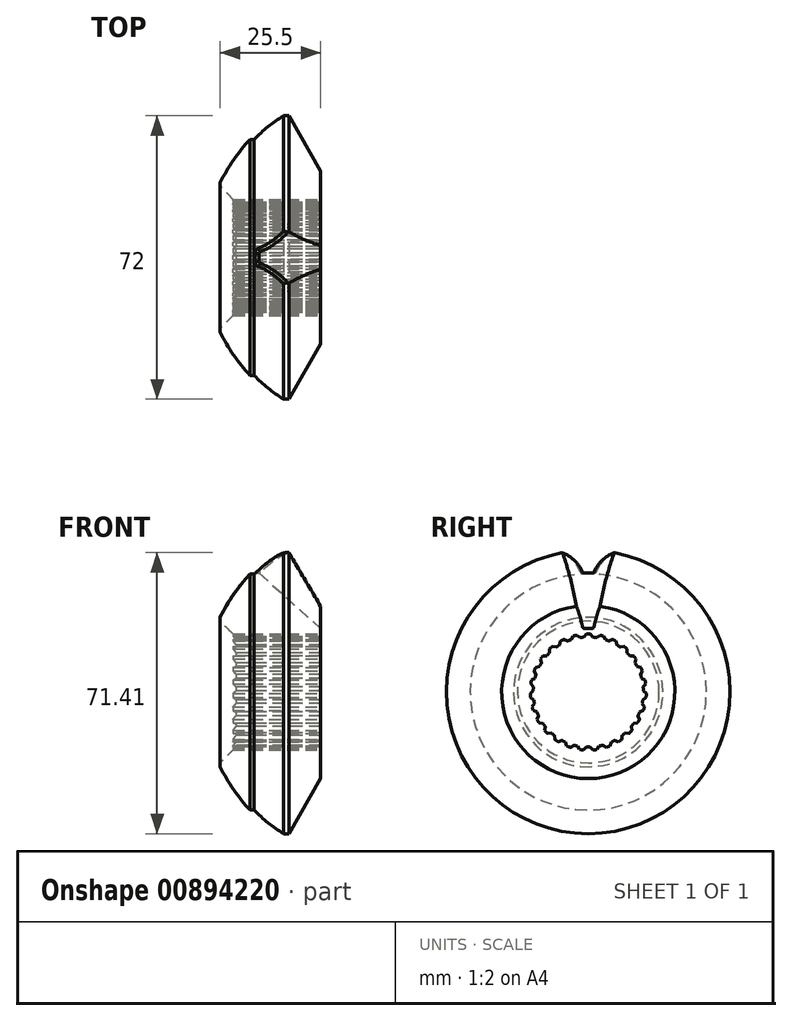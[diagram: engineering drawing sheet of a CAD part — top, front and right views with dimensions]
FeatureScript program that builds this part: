
annotation { "Feature Type Name" : "Feature", "Feature Type Description" : "" }
export const myFeature = defineFeature(function(context is Context, id is Id, definition is map)
    precondition{}
    {
        {
            var Q0;
            Q0=qCreatedBy(makeId("Front.planeOp"),FACE);
            var sketch = newSketch(context, id + "F0", { "sketchPlane" : qUnion([Q0])});
            skLineSegment(sketch, "E0", {"start": v(-35.13, 14) * mm, "end": v(-13.63, 14) * mm});
            skLineSegment(sketch, "E1", {"start": v(-13.63, 14) * mm, "end": v(-13.63, 22) * mm});
            skLineSegment(sketch, "E2", {"start": v(-13.63, 22) * mm, "end": v(-21.71, 36) * mm});
            skLineSegment(sketch, "E3", {"start": v(-21.71, 36) * mm, "end": v(-23.11, 36) * mm});
            skLineSegment(sketch, "E4", {"start": v(-35.13, 14) * mm, "end": v(-39.13, 18) * mm});
            skLineSegment(sketch, "E5", {"start": v(-39.13, 18) * mm, "end": v(-39.13, 19) * mm});
            skArc(sketch, "E6", {"start": v(-31.5, 30) * mm, "mid": v(-35.74, 24.8) * mm, "end": v(-39.13, 19) * mm});
            skLineSegment(sketch, "E7", {"start": v(-31.5, 30) * mm, "end": v(-30.5, 30) * mm});
            skArc(sketch, "E8", {"start": v(-23.11, 36) * mm, "mid": v(-26.97, 33.2) * mm, "end": v(-30.5, 30) * mm});
            skLineSegment(sketch, "E9", {"start": v(-39.13, 0) * mm, "end": v(0, 0) * mm});
            skSolve(sketch);
        }
        {
            var Q0;
            Q0=makeQuery(id+"F0.imprint","IMPRINT",FACE,{"disambiguationData":[TD([[makeQuery(id+"F0.imprint","IMPRINT",EDGE,{"derivedFrom":sQuery(id+"F0.wireOp",EDGE,"E0")}),1.0]])]});
            var Q1;
            Q1=sQuery(id+"F0.wireOp",EDGE,"E9");
            revolve(context, id + "F1", {"surfaceOperationType" : NewSurfaceOperationType.NEW, "entities" : qUnion([Q0]), "axis" : qUnion([Q1]), "revolveType" : RevolveType.FULL});
        }
        {
            var Q0;
            Q0=makeQuery(id+"F1.opRevolve","SWEPT_FACE",FACE,{"disambiguationData":[OSD([sQuery(id+"F0.wireOp",EDGE,"E1")])]});
            var sketch = newSketch(context, id + "F2", { "sketchPlane" : qUnion([Q0])});
            skLineSegment(sketch, "E10", {"start": v(0, 0) * mm, "end": v(0, 16.12) * mm, "construction": true});
            skLineSegment(sketch, "E11", {"start": v(0, 16.12) * mm, "end": v(20, 16.12) * mm, "construction": true});
            skSolve(sketch);
        }
        {
            var Q0;
            Q0=sQuery(id+"F2.wireOp",EDGE,"E11");
            var Q1;
            {var subQ0=sQuery(id+"F0.wireOp",EDGE,"E1");Q1=makeQuery(id+"F2.imprint","IMPRINT",FACE,{"disambiguationData":[TD([[makeQuery(id+"F2.imprint","IMPRINT",EDGE,{"derivedFrom":makeQuery(id+"F1.opRevolve","SWEPT_EDGE",EDGE,{"disambiguationData":[OSD([sQuery(id+"F0.wireOp",EDGE,"E0"),subQ0])]})}),1.0]])]});}
            cPlane(context, id + "F3", {"entities" : qUnion([Q0, Q1]), "cplaneType" : CPlaneType.LINE_ANGLE, "offset" : 25 * mm, "angle" : 42 * degree, "width" : 150 * mm, "height" : 150 * mm});
        }
        {
            var Q0;
            Q0=qCreatedBy(id+"F3.planeOp",FACE);
            var sketch = newSketch(context, id + "F4", { "sketchPlane" : qUnion([Q0])});
            skLineSegment(sketch, "E12", {"start": v(0, 2.86) * mm, "end": v(0, 7.08) * mm, "construction": true});
            skLineSegment(sketch, "E13", {"start": v(3, 7.08) * mm, "end": v(-3, 7.08) * mm, "construction": true});
            skLineSegment(sketch, "E14", {"start": v(6.55, 11.78) * mm, "end": v(-6.55, 11.78) * mm, "construction": true});
            skLineSegment(sketch, "E15", {"start": v(0, 7.08) * mm, "end": v(0, 11.78) * mm, "construction": true});
            skArc(sketch, "E16", {"start": v(-1.48, 3.23) * mm, "mid": v(-2.13, 5.2) * mm, "end": v(-3, 7.08) * mm});
            skArc(sketch, "E17", {"start": v(-3, 7.08) * mm, "mid": v(-4.59, 9.57) * mm, "end": v(-6.55, 11.78) * mm});
            skArc(sketch, "E18", {"start": v(-1.48, 3.23) * mm, "mid": v(-1.3, 2.97) * mm, "end": v(-1, 2.86) * mm});
            skLineSegment(sketch, "E19", {"start": v(-1, 2.86) * mm, "end": v(1, 2.86) * mm});
            skLineSegment(sketch, "E20", {"start": v(-6.55, 11.78) * mm, "end": v(-6.55, 12.78) * mm});
            skLineSegment(sketch, "E21", {"start": v(-6.55, 12.78) * mm, "end": v(6.55, 12.78) * mm});
            skLineSegment(sketch, "E22", {"start": v(6.55, 12.78) * mm, "end": v(6.55, 11.78) * mm});
            skArc(sketch, "E23", {"start": v(1, 2.86) * mm, "mid": v(1.3, 2.97) * mm, "end": v(1.48, 3.23) * mm});
            skArc(sketch, "E24", {"start": v(3, 7.08) * mm, "mid": v(2.13, 5.2) * mm, "end": v(1.48, 3.23) * mm});
            skArc(sketch, "E25", {"start": v(6.55, 11.78) * mm, "mid": v(4.59, 9.57) * mm, "end": v(3, 7.08) * mm});
            skSolve(sketch);
        }
        {
            var Q0;
            Q0=makeQuery(id+"F4.imprint","IMPRINT",FACE,{"disambiguationData":[TD([[makeQuery(id+"F4.imprint","IMPRINT",EDGE,{"derivedFrom":sQuery(id+"F4.wireOp",EDGE,"E16")}),-1.0]])]});
            extrude(context, id + "F5", {"entities" : qUnion([Q0]), "operationType" : NewBodyOperationType.REMOVE, "endBound" : BoundingType.THROUGH_ALL, "depth" : 25 * mm, "offsetDistance" : 25 * mm});
        }
        {
            var Q0;
            Q0=makeQuery(id+"F5.boolean.opBoolean","INTERSECT",EDGE,{"derivedFrom":[makeQuery(id+"F1.opRevolve","SWEPT_FACE",FACE,{"disambiguationData":[OSD([sQuery(id+"F0.wireOp",EDGE,"E8")])]}),makeQuery(id+"F5.opExtrude","SWEPT_FACE",FACE,{"disambiguationData":[OSD([sQuery(id+"F4.wireOp",EDGE,"E16"),sQuery(id+"F4.wireOp",EDGE,"E17")])]})]});
            var Q1;
            Q1=makeQuery(id+"Ff50wVPIjlx40M6_1.1.F5.boolean.opBoolean","INTERSECT",EDGE,{"derivedFrom":[makeQuery(id+"F1.opRevolve","SWEPT_FACE",FACE,{"disambiguationData":[OSD([sQuery(id+"F0.wireOp",EDGE,"E8")])]}),makeQuery(id+"Ff50wVPIjlx40M6_1.1.F5.opExtrude","SWEPT_FACE",FACE,{"disambiguationData":[OSD([sQuery(id+"F4.wireOp",EDGE,"E16"),sQuery(id+"F4.wireOp",EDGE,"E17")])]})]});
            var Q2;
            Q2=makeQuery(id+"Ff50wVPIjlx40M6_1.2.F5.boolean.opBoolean","INTERSECT",EDGE,{"derivedFrom":[makeQuery(id+"F1.opRevolve","SWEPT_FACE",FACE,{"disambiguationData":[OSD([sQuery(id+"F0.wireOp",EDGE,"E8")])]}),makeQuery(id+"Ff50wVPIjlx40M6_1.2.F5.opExtrude","SWEPT_FACE",FACE,{"disambiguationData":[OSD([sQuery(id+"F4.wireOp",EDGE,"E16"),sQuery(id+"F4.wireOp",EDGE,"E17")])]})]});
            var Q3;
            Q3=makeQuery(id+"Ff50wVPIjlx40M6_1.3.F5.boolean.opBoolean","INTERSECT",EDGE,{"derivedFrom":[makeQuery(id+"F1.opRevolve","SWEPT_FACE",FACE,{"disambiguationData":[OSD([sQuery(id+"F0.wireOp",EDGE,"E8")])]}),makeQuery(id+"Ff50wVPIjlx40M6_1.3.F5.opExtrude","SWEPT_FACE",FACE,{"disambiguationData":[OSD([sQuery(id+"F4.wireOp",EDGE,"E16"),sQuery(id+"F4.wireOp",EDGE,"E17")])]})]});
            var Q4;
            Q4=makeQuery(id+"Ff50wVPIjlx40M6_1.4.F5.boolean.opBoolean","INTERSECT",EDGE,{"derivedFrom":[makeQuery(id+"F1.opRevolve","SWEPT_FACE",FACE,{"disambiguationData":[OSD([sQuery(id+"F0.wireOp",EDGE,"E8")])]}),makeQuery(id+"Ff50wVPIjlx40M6_1.4.F5.opExtrude","SWEPT_FACE",FACE,{"disambiguationData":[OSD([sQuery(id+"F4.wireOp",EDGE,"E16"),sQuery(id+"F4.wireOp",EDGE,"E17")])]})]});
            var Q5;
            Q5=makeQuery(id+"Ff50wVPIjlx40M6_1.5.F5.boolean.opBoolean","INTERSECT",EDGE,{"derivedFrom":[makeQuery(id+"F1.opRevolve","SWEPT_FACE",FACE,{"disambiguationData":[OSD([sQuery(id+"F0.wireOp",EDGE,"E8")])]}),makeQuery(id+"Ff50wVPIjlx40M6_1.5.F5.opExtrude","SWEPT_FACE",FACE,{"disambiguationData":[OSD([sQuery(id+"F4.wireOp",EDGE,"E16"),sQuery(id+"F4.wireOp",EDGE,"E17")])]})]});
            var Q6;
            Q6=makeQuery(id+"Ff50wVPIjlx40M6_1.6.F5.boolean.opBoolean","INTERSECT",EDGE,{"derivedFrom":[makeQuery(id+"F1.opRevolve","SWEPT_FACE",FACE,{"disambiguationData":[OSD([sQuery(id+"F0.wireOp",EDGE,"E8")])]}),makeQuery(id+"Ff50wVPIjlx40M6_1.6.F5.opExtrude","SWEPT_FACE",FACE,{"disambiguationData":[OSD([sQuery(id+"F4.wireOp",EDGE,"E16"),sQuery(id+"F4.wireOp",EDGE,"E17")])]})]});
            var Q7;
            Q7=makeQuery(id+"Ff50wVPIjlx40M6_1.7.F5.boolean.opBoolean","INTERSECT",EDGE,{"derivedFrom":[makeQuery(id+"F1.opRevolve","SWEPT_FACE",FACE,{"disambiguationData":[OSD([sQuery(id+"F0.wireOp",EDGE,"E8")])]}),makeQuery(id+"Ff50wVPIjlx40M6_1.7.F5.opExtrude","SWEPT_FACE",FACE,{"disambiguationData":[OSD([sQuery(id+"F4.wireOp",EDGE,"E16"),sQuery(id+"F4.wireOp",EDGE,"E17")])]})]});
            var Q8;
            Q8=makeQuery(id+"Ff50wVPIjlx40M6_1.8.F5.boolean.opBoolean","INTERSECT",EDGE,{"derivedFrom":[makeQuery(id+"F1.opRevolve","SWEPT_FACE",FACE,{"disambiguationData":[OSD([sQuery(id+"F0.wireOp",EDGE,"E8")])]}),makeQuery(id+"Ff50wVPIjlx40M6_1.8.F5.opExtrude","SWEPT_FACE",FACE,{"disambiguationData":[OSD([sQuery(id+"F4.wireOp",EDGE,"E16"),sQuery(id+"F4.wireOp",EDGE,"E17")])]})]});
            var Q9;
            Q9=makeQuery(id+"Ff50wVPIjlx40M6_1.9.F5.boolean.opBoolean","INTERSECT",EDGE,{"derivedFrom":[makeQuery(id+"F1.opRevolve","SWEPT_FACE",FACE,{"disambiguationData":[OSD([sQuery(id+"F0.wireOp",EDGE,"E8")])]}),makeQuery(id+"Ff50wVPIjlx40M6_1.9.F5.opExtrude","SWEPT_FACE",FACE,{"disambiguationData":[OSD([sQuery(id+"F4.wireOp",EDGE,"E16"),sQuery(id+"F4.wireOp",EDGE,"E17")])]})]});
            var Q10;
            Q10=makeQuery(id+"Ff50wVPIjlx40M6_1.10.F5.boolean.opBoolean","INTERSECT",EDGE,{"derivedFrom":[makeQuery(id+"F1.opRevolve","SWEPT_FACE",FACE,{"disambiguationData":[OSD([sQuery(id+"F0.wireOp",EDGE,"E8")])]}),makeQuery(id+"Ff50wVPIjlx40M6_1.10.F5.opExtrude","SWEPT_FACE",FACE,{"disambiguationData":[OSD([sQuery(id+"F4.wireOp",EDGE,"E16"),sQuery(id+"F4.wireOp",EDGE,"E17")])]})]});
            var Q11;
            Q11=makeQuery(id+"Ff50wVPIjlx40M6_1.11.F5.boolean.opBoolean","INTERSECT",EDGE,{"derivedFrom":[makeQuery(id+"F1.opRevolve","SWEPT_FACE",FACE,{"disambiguationData":[OSD([sQuery(id+"F0.wireOp",EDGE,"E8")])]}),makeQuery(id+"Ff50wVPIjlx40M6_1.11.F5.opExtrude","SWEPT_FACE",FACE,{"disambiguationData":[OSD([sQuery(id+"F4.wireOp",EDGE,"E16"),sQuery(id+"F4.wireOp",EDGE,"E17")])]})]});
            var Q12;
            Q12=makeQuery(id+"Ff50wVPIjlx40M6_1.12.F5.boolean.opBoolean","INTERSECT",EDGE,{"derivedFrom":[makeQuery(id+"F1.opRevolve","SWEPT_FACE",FACE,{"disambiguationData":[OSD([sQuery(id+"F0.wireOp",EDGE,"E8")])]}),makeQuery(id+"Ff50wVPIjlx40M6_1.12.F5.opExtrude","SWEPT_FACE",FACE,{"disambiguationData":[OSD([sQuery(id+"F4.wireOp",EDGE,"E16"),sQuery(id+"F4.wireOp",EDGE,"E17")])]})]});
            var Q13;
            Q13=makeQuery(id+"Ff50wVPIjlx40M6_1.13.F5.boolean.opBoolean","INTERSECT",EDGE,{"derivedFrom":[makeQuery(id+"F1.opRevolve","SWEPT_FACE",FACE,{"disambiguationData":[OSD([sQuery(id+"F0.wireOp",EDGE,"E8")])]}),makeQuery(id+"Ff50wVPIjlx40M6_1.13.F5.opExtrude","SWEPT_FACE",FACE,{"disambiguationData":[OSD([sQuery(id+"F4.wireOp",EDGE,"E16"),sQuery(id+"F4.wireOp",EDGE,"E17")])]})]});
            chamfer(context, id + "F6", {"entities" : qUnion([Q0, Q1, Q2, Q3, Q4, Q5, Q6, Q7, Q8, Q9, Q10, Q11, Q12, Q13]), "width" : 0.75 * mm, "tangentPropagation" : true});
        }
        {
            var Q0;
            Q0=makeQuery(id+"F1.opRevolve","SWEPT_FACE",FACE,{"disambiguationData":[OSD([sQuery(id+"F0.wireOp",EDGE,"E1")])]});
            var sketch = newSketch(context, id + "F7", { "sketchPlane" : qUnion([Q0])});
            skArc(sketch, "E26", {"start": v(0.5, 14.72) * mm, "mid": v(0.25, 14.72) * mm, "end": v(0, 14.72) * mm});
            skArc(sketch, "E27", {"start": v(1.6, 13.58) * mm, "mid": v(1.5, 13.6) * mm, "end": v(1.4, 13.6) * mm});
            skLineSegment(sketch, "E28", {"start": v(1.4, 13.6) * mm, "end": v(0.5, 14.72) * mm});
            skArc(sketch, "E29", {"start": v(0, 14.72) * mm, "mid": v(-0.25, 14.72) * mm, "end": v(-0.5, 14.72) * mm});
            skArc(sketch, "E30", {"start": v(-1.4, 13.6) * mm, "mid": v(-1.5, 13.6) * mm, "end": v(-1.6, 13.58) * mm});
            skLineSegment(sketch, "E31", {"start": v(-1.4, 13.6) * mm, "end": v(-0.5, 14.72) * mm});
            skArc(sketch, "E32", {"start": v(-2.91, 14.43) * mm, "mid": v(-3.16, 14.38) * mm, "end": v(-3.4, 14.33) * mm});
            skArc(sketch, "E33", {"start": v(-1.6, 13.58) * mm, "mid": v(-1.69, 13.57) * mm, "end": v(-1.79, 13.56) * mm});
            skLineSegment(sketch, "E34", {"start": v(-1.79, 13.56) * mm, "end": v(-2.91, 14.43) * mm});
            skArc(sketch, "E35", {"start": v(-3.4, 14.33) * mm, "mid": v(-3.64, 14.27) * mm, "end": v(-3.89, 14.2) * mm});
            skArc(sketch, "E36", {"start": v(-4.5, 12.92) * mm, "mid": v(-4.6, 12.88) * mm, "end": v(-4.69, 12.85) * mm});
            skLineSegment(sketch, "E37", {"start": v(-4.5, 12.92) * mm, "end": v(-3.89, 14.2) * mm});
            skArc(sketch, "E38", {"start": v(-6.17, 13.37) * mm, "mid": v(-6.4, 13.27) * mm, "end": v(-6.62, 13.16) * mm});
            skArc(sketch, "E39", {"start": v(-4.69, 12.85) * mm, "mid": v(-4.78, 12.81) * mm, "end": v(-4.87, 12.78) * mm});
            skLineSegment(sketch, "E40", {"start": v(-4.87, 12.78) * mm, "end": v(-6.17, 13.37) * mm});
            skArc(sketch, "E41", {"start": v(-6.62, 13.16) * mm, "mid": v(-6.84, 13.04) * mm, "end": v(-7.06, 12.92) * mm});
            skArc(sketch, "E42", {"start": v(-7.36, 11.53) * mm, "mid": v(-7.44, 11.48) * mm, "end": v(-7.53, 11.42) * mm});
            skLineSegment(sketch, "E43", {"start": v(-7.36, 11.53) * mm, "end": v(-7.06, 12.92) * mm});
            skArc(sketch, "E44", {"start": v(-9.1, 11.59) * mm, "mid": v(-9.29, 11.43) * mm, "end": v(-9.48, 11.27) * mm});
            skArc(sketch, "E45", {"start": v(-7.53, 11.42) * mm, "mid": v(-7.61, 11.37) * mm, "end": v(-7.7, 11.31) * mm});
            skLineSegment(sketch, "E46", {"start": v(-7.7, 11.31) * mm, "end": v(-9.1, 11.59) * mm});
            skArc(sketch, "E47", {"start": v(-9.48, 11.27) * mm, "mid": v(-9.67, 11.11) * mm, "end": v(-9.86, 10.95) * mm});
            skArc(sketch, "E48", {"start": v(-9.83, 9.52) * mm, "mid": v(-9.9, 9.45) * mm, "end": v(-9.97, 9.38) * mm});
            skLineSegment(sketch, "E49", {"start": v(-9.83, 9.52) * mm, "end": v(-9.86, 10.95) * mm});
            skArc(sketch, "E50", {"start": v(-11.53, 9.18) * mm, "mid": v(-11.68, 8.98) * mm, "end": v(-11.83, 8.78) * mm});
            skArc(sketch, "E51", {"start": v(-9.97, 9.38) * mm, "mid": v(-10.03, 9.3) * mm, "end": v(-10.1, 9.23) * mm});
            skLineSegment(sketch, "E52", {"start": v(-10.1, 9.23) * mm, "end": v(-11.53, 9.18) * mm});
            skArc(sketch, "E53", {"start": v(-11.83, 8.78) * mm, "mid": v(-11.98, 8.58) * mm, "end": v(-12.12, 8.38) * mm});
            skArc(sketch, "E54", {"start": v(-11.76, 7) * mm, "mid": v(-11.81, 6.91) * mm, "end": v(-11.86, 6.82) * mm});
            skLineSegment(sketch, "E55", {"start": v(-11.76, 7) * mm, "end": v(-12.12, 8.38) * mm});
            skArc(sketch, "E56", {"start": v(-13.34, 6.27) * mm, "mid": v(-13.44, 6.05) * mm, "end": v(-13.54, 5.82) * mm});
            skArc(sketch, "E57", {"start": v(-11.86, 6.82) * mm, "mid": v(-11.91, 6.74) * mm, "end": v(-11.96, 6.65) * mm});
            skLineSegment(sketch, "E58", {"start": v(-11.96, 6.65) * mm, "end": v(-13.34, 6.27) * mm});
            skArc(sketch, "E59", {"start": v(-13.54, 5.82) * mm, "mid": v(-13.64, 5.59) * mm, "end": v(-13.73, 5.35) * mm});
            skArc(sketch, "E60", {"start": v(-13.07, 4.1) * mm, "mid": v(-13.1, 4) * mm, "end": v(-13.12, 3.9) * mm});
            skLineSegment(sketch, "E61", {"start": v(-13.07, 4.1) * mm, "end": v(-13.73, 5.35) * mm});
            skArc(sketch, "E62", {"start": v(-14.43, 3.03) * mm, "mid": v(-14.48, 2.78) * mm, "end": v(-14.53, 2.54) * mm});
            skArc(sketch, "E63", {"start": v(-13.12, 3.9) * mm, "mid": v(-13.15, 3.8) * mm, "end": v(-13.18, 3.71) * mm});
            skLineSegment(sketch, "E64", {"start": v(-13.18, 3.71) * mm, "end": v(-14.43, 3.03) * mm});
            skArc(sketch, "E65", {"start": v(-14.53, 2.54) * mm, "mid": v(-14.57, 2.29) * mm, "end": v(-14.6, 2.04) * mm});
            skArc(sketch, "E66", {"start": v(-13.66, 0.97) * mm, "mid": v(-13.67, 0.87) * mm, "end": v(-13.68, 0.77) * mm});
            skLineSegment(sketch, "E67", {"start": v(-13.66, 0.97) * mm, "end": v(-14.6, 2.04) * mm});
            skArc(sketch, "E68", {"start": v(-14.75, -0.38) * mm, "mid": v(-14.74, -0.63) * mm, "end": v(-14.73, -0.88) * mm});
            skArc(sketch, "E69", {"start": v(-13.68, 0.77) * mm, "mid": v(-13.68, 0.67) * mm, "end": v(-13.69, 0.57) * mm});
            skLineSegment(sketch, "E70", {"start": v(-13.69, 0.57) * mm, "end": v(-14.75, -0.38) * mm});
            skArc(sketch, "E71", {"start": v(-14.73, -0.88) * mm, "mid": v(-14.7, -1.13) * mm, "end": v(-14.69, -1.38) * mm});
            skArc(sketch, "E72", {"start": v(-13.53, -2.2) * mm, "mid": v(-13.5, -2.3) * mm, "end": v(-13.5, -2.4) * mm});
            skLineSegment(sketch, "E73", {"start": v(-13.53, -2.2) * mm, "end": v(-14.69, -1.38) * mm});
            skArc(sketch, "E74", {"start": v(-14.27, -3.77) * mm, "mid": v(-14.2, -4.02) * mm, "end": v(-14.13, -4.26) * mm});
            skArc(sketch, "E75", {"start": v(-13.5, -2.4) * mm, "mid": v(-13.47, -2.5) * mm, "end": v(-13.46, -2.6) * mm});
            skLineSegment(sketch, "E76", {"start": v(-13.46, -2.6) * mm, "end": v(-14.27, -3.77) * mm});
            skArc(sketch, "E77", {"start": v(-14.13, -4.26) * mm, "mid": v(-14.06, -4.5) * mm, "end": v(-13.98, -4.73) * mm});
            skArc(sketch, "E78", {"start": v(-12.66, -5.27) * mm, "mid": v(-12.62, -5.36) * mm, "end": v(-12.58, -5.45) * mm});
            skLineSegment(sketch, "E79", {"start": v(-12.66, -5.27) * mm, "end": v(-13.98, -4.73) * mm});
            skArc(sketch, "E80", {"start": v(-13.02, -6.96) * mm, "mid": v(-12.9, -7.18) * mm, "end": v(-12.77, -7.4) * mm});
            skArc(sketch, "E81", {"start": v(-12.58, -5.45) * mm, "mid": v(-12.54, -5.54) * mm, "end": v(-12.5, -5.63) * mm});
            skLineSegment(sketch, "E82", {"start": v(-12.5, -5.63) * mm, "end": v(-13.02, -6.96) * mm});
            skArc(sketch, "E83", {"start": v(-12.77, -7.4) * mm, "mid": v(-12.65, -7.62) * mm, "end": v(-12.52, -7.83) * mm});
            skArc(sketch, "E84", {"start": v(-11.1, -8.04) * mm, "mid": v(-11.05, -8.13) * mm, "end": v(-10.99, -8.2) * mm});
            skLineSegment(sketch, "E85", {"start": v(-11.1, -8.04) * mm, "end": v(-12.52, -7.83) * mm});
            skArc(sketch, "E86", {"start": v(-11.07, -9.78) * mm, "mid": v(-10.9, -9.96) * mm, "end": v(-10.73, -10.15) * mm});
            skArc(sketch, "E87", {"start": v(-10.99, -8.2) * mm, "mid": v(-10.93, -8.29) * mm, "end": v(-10.87, -8.37) * mm});
            skLineSegment(sketch, "E88", {"start": v(-10.87, -8.37) * mm, "end": v(-11.07, -9.78) * mm});
            skArc(sketch, "E89", {"start": v(-10.73, -10.15) * mm, "mid": v(-10.56, -10.33) * mm, "end": v(-10.38, -10.5) * mm});
            skArc(sketch, "E90", {"start": v(-8.96, -10.4) * mm, "mid": v(-8.88, -10.46) * mm, "end": v(-8.8, -10.52) * mm});
            skLineSegment(sketch, "E91", {"start": v(-8.96, -10.4) * mm, "end": v(-10.38, -10.5) * mm});
            skArc(sketch, "E92", {"start": v(-8.52, -12.07) * mm, "mid": v(-8.31, -12.2) * mm, "end": v(-8.1, -12.35) * mm});
            skArc(sketch, "E93", {"start": v(-8.8, -10.52) * mm, "mid": v(-8.73, -10.58) * mm, "end": v(-8.65, -10.65) * mm});
            skLineSegment(sketch, "E94", {"start": v(-8.65, -10.65) * mm, "end": v(-8.52, -12.07) * mm});
            skArc(sketch, "E95", {"start": v(-8.1, -12.35) * mm, "mid": v(-7.9, -12.48) * mm, "end": v(-7.68, -12.62) * mm});
            skArc(sketch, "E96", {"start": v(-6.33, -12.18) * mm, "mid": v(-6.24, -12.22) * mm, "end": v(-6.15, -12.27) * mm});
            skLineSegment(sketch, "E97", {"start": v(-6.33, -12.18) * mm, "end": v(-7.68, -12.62) * mm});
            skArc(sketch, "E98", {"start": v(-5.51, -13.7) * mm, "mid": v(-5.28, -13.8) * mm, "end": v(-5.04, -13.89) * mm});
            skArc(sketch, "E99", {"start": v(-6.15, -12.27) * mm, "mid": v(-6.06, -12.31) * mm, "end": v(-5.97, -12.36) * mm});
            skLineSegment(sketch, "E100", {"start": v(-5.97, -12.36) * mm, "end": v(-5.51, -13.7) * mm});
            skArc(sketch, "E101", {"start": v(-5.04, -13.89) * mm, "mid": v(-4.8, -13.97) * mm, "end": v(-4.57, -14.05) * mm});
            skArc(sketch, "E102", {"start": v(-3.35, -13.3) * mm, "mid": v(-3.26, -13.33) * mm, "end": v(-3.16, -13.36) * mm});
            skLineSegment(sketch, "E103", {"start": v(-3.35, -13.3) * mm, "end": v(-4.57, -14.05) * mm});
            skArc(sketch, "E104", {"start": v(-2.2, -14.6) * mm, "mid": v(-1.96, -14.64) * mm, "end": v(-1.71, -14.68) * mm});
            skArc(sketch, "E105", {"start": v(-3.16, -13.36) * mm, "mid": v(-3.06, -13.38) * mm, "end": v(-2.96, -13.4) * mm});
            skLineSegment(sketch, "E106", {"start": v(-2.96, -13.4) * mm, "end": v(-2.2, -14.6) * mm});
            skArc(sketch, "E107", {"start": v(-1.71, -14.68) * mm, "mid": v(-1.46, -14.7) * mm, "end": v(-1.21, -14.72) * mm});
            skArc(sketch, "E108", {"start": v(-0.2, -13.72) * mm, "mid": v(-0.1, -13.72) * mm, "end": v(0, -13.73) * mm});
            skLineSegment(sketch, "E109", {"start": v(-0.2, -13.72) * mm, "end": v(-1.21, -14.72) * mm});
            skArc(sketch, "E110", {"start": v(1.21, -14.72) * mm, "mid": v(1.46, -14.7) * mm, "end": v(1.71, -14.68) * mm});
            skArc(sketch, "E111", {"start": v(0, -13.73) * mm, "mid": v(0.1, -13.72) * mm, "end": v(0.2, -13.72) * mm});
            skLineSegment(sketch, "E112", {"start": v(0.2, -13.72) * mm, "end": v(1.21, -14.72) * mm});
            skArc(sketch, "E113", {"start": v(1.71, -14.68) * mm, "mid": v(1.96, -14.64) * mm, "end": v(2.2, -14.6) * mm});
            skArc(sketch, "E114", {"start": v(2.96, -13.4) * mm, "mid": v(3.06, -13.38) * mm, "end": v(3.16, -13.36) * mm});
            skLineSegment(sketch, "E115", {"start": v(2.96, -13.4) * mm, "end": v(2.2, -14.6) * mm});
            skArc(sketch, "E116", {"start": v(4.57, -14.05) * mm, "mid": v(4.8, -13.97) * mm, "end": v(5.04, -13.89) * mm});
            skArc(sketch, "E117", {"start": v(3.16, -13.36) * mm, "mid": v(3.26, -13.33) * mm, "end": v(3.35, -13.3) * mm});
            skLineSegment(sketch, "E118", {"start": v(3.35, -13.3) * mm, "end": v(4.57, -14.05) * mm});
            skArc(sketch, "E119", {"start": v(5.04, -13.89) * mm, "mid": v(5.28, -13.8) * mm, "end": v(5.51, -13.7) * mm});
            skArc(sketch, "E120", {"start": v(5.97, -12.36) * mm, "mid": v(6.06, -12.31) * mm, "end": v(6.15, -12.27) * mm});
            skLineSegment(sketch, "E121", {"start": v(5.97, -12.36) * mm, "end": v(5.51, -13.7) * mm});
            skArc(sketch, "E122", {"start": v(7.68, -12.62) * mm, "mid": v(7.9, -12.48) * mm, "end": v(8.1, -12.35) * mm});
            skArc(sketch, "E123", {"start": v(6.15, -12.27) * mm, "mid": v(6.24, -12.22) * mm, "end": v(6.33, -12.18) * mm});
            skLineSegment(sketch, "E124", {"start": v(6.33, -12.18) * mm, "end": v(7.68, -12.62) * mm});
            skArc(sketch, "E125", {"start": v(8.1, -12.35) * mm, "mid": v(8.31, -12.2) * mm, "end": v(8.52, -12.07) * mm});
            skArc(sketch, "E126", {"start": v(8.65, -10.65) * mm, "mid": v(8.73, -10.58) * mm, "end": v(8.8, -10.52) * mm});
            skLineSegment(sketch, "E127", {"start": v(8.65, -10.65) * mm, "end": v(8.52, -12.07) * mm});
            skArc(sketch, "E128", {"start": v(10.38, -10.5) * mm, "mid": v(10.56, -10.33) * mm, "end": v(10.73, -10.15) * mm});
            skArc(sketch, "E129", {"start": v(8.8, -10.52) * mm, "mid": v(8.88, -10.46) * mm, "end": v(8.96, -10.4) * mm});
            skLineSegment(sketch, "E130", {"start": v(8.96, -10.4) * mm, "end": v(10.38, -10.5) * mm});
            skArc(sketch, "E131", {"start": v(10.73, -10.15) * mm, "mid": v(10.9, -9.96) * mm, "end": v(11.07, -9.78) * mm});
            skArc(sketch, "E132", {"start": v(10.87, -8.37) * mm, "mid": v(10.93, -8.29) * mm, "end": v(10.99, -8.2) * mm});
            skLineSegment(sketch, "E133", {"start": v(10.87, -8.37) * mm, "end": v(11.07, -9.78) * mm});
            skArc(sketch, "E134", {"start": v(12.52, -7.83) * mm, "mid": v(12.65, -7.62) * mm, "end": v(12.77, -7.4) * mm});
            skArc(sketch, "E135", {"start": v(10.99, -8.2) * mm, "mid": v(11.05, -8.13) * mm, "end": v(11.1, -8.04) * mm});
            skLineSegment(sketch, "E136", {"start": v(11.1, -8.04) * mm, "end": v(12.52, -7.83) * mm});
            skArc(sketch, "E137", {"start": v(12.77, -7.4) * mm, "mid": v(12.9, -7.18) * mm, "end": v(13.02, -6.96) * mm});
            skArc(sketch, "E138", {"start": v(12.5, -5.63) * mm, "mid": v(12.54, -5.54) * mm, "end": v(12.58, -5.45) * mm});
            skLineSegment(sketch, "E139", {"start": v(12.5, -5.63) * mm, "end": v(13.02, -6.96) * mm});
            skArc(sketch, "E140", {"start": v(13.98, -4.73) * mm, "mid": v(14.06, -4.5) * mm, "end": v(14.13, -4.26) * mm});
            skArc(sketch, "E141", {"start": v(12.58, -5.45) * mm, "mid": v(12.62, -5.36) * mm, "end": v(12.66, -5.27) * mm});
            skLineSegment(sketch, "E142", {"start": v(12.66, -5.27) * mm, "end": v(13.98, -4.73) * mm});
            skArc(sketch, "E143", {"start": v(14.13, -4.26) * mm, "mid": v(14.2, -4.02) * mm, "end": v(14.27, -3.77) * mm});
            skArc(sketch, "E144", {"start": v(13.46, -2.6) * mm, "mid": v(13.47, -2.5) * mm, "end": v(13.5, -2.4) * mm});
            skLineSegment(sketch, "E145", {"start": v(13.46, -2.6) * mm, "end": v(14.27, -3.77) * mm});
            skArc(sketch, "E146", {"start": v(14.69, -1.38) * mm, "mid": v(14.7, -1.13) * mm, "end": v(14.73, -0.88) * mm});
            skArc(sketch, "E147", {"start": v(13.5, -2.4) * mm, "mid": v(13.5, -2.3) * mm, "end": v(13.53, -2.2) * mm});
            skLineSegment(sketch, "E148", {"start": v(13.53, -2.2) * mm, "end": v(14.69, -1.38) * mm});
            skArc(sketch, "E149", {"start": v(14.73, -0.88) * mm, "mid": v(14.74, -0.63) * mm, "end": v(14.75, -0.38) * mm});
            skArc(sketch, "E150", {"start": v(13.69, 0.57) * mm, "mid": v(13.68, 0.67) * mm, "end": v(13.68, 0.77) * mm});
            skLineSegment(sketch, "E151", {"start": v(13.69, 0.57) * mm, "end": v(14.75, -0.38) * mm});
            skArc(sketch, "E152", {"start": v(14.6, 2.04) * mm, "mid": v(14.57, 2.29) * mm, "end": v(14.53, 2.54) * mm});
            skArc(sketch, "E153", {"start": v(13.68, 0.77) * mm, "mid": v(13.67, 0.87) * mm, "end": v(13.66, 0.97) * mm});
            skLineSegment(sketch, "E154", {"start": v(13.66, 0.97) * mm, "end": v(14.6, 2.04) * mm});
            skArc(sketch, "E155", {"start": v(14.53, 2.54) * mm, "mid": v(14.48, 2.78) * mm, "end": v(14.43, 3.03) * mm});
            skArc(sketch, "E156", {"start": v(13.18, 3.71) * mm, "mid": v(13.15, 3.8) * mm, "end": v(13.12, 3.9) * mm});
            skLineSegment(sketch, "E157", {"start": v(13.18, 3.71) * mm, "end": v(14.43, 3.03) * mm});
            skArc(sketch, "E158", {"start": v(13.73, 5.35) * mm, "mid": v(13.64, 5.59) * mm, "end": v(13.54, 5.82) * mm});
            skArc(sketch, "E159", {"start": v(13.12, 3.9) * mm, "mid": v(13.1, 4) * mm, "end": v(13.07, 4.1) * mm});
            skLineSegment(sketch, "E160", {"start": v(13.07, 4.1) * mm, "end": v(13.73, 5.35) * mm});
            skArc(sketch, "E161", {"start": v(13.54, 5.82) * mm, "mid": v(13.44, 6.05) * mm, "end": v(13.34, 6.27) * mm});
            skArc(sketch, "E162", {"start": v(11.96, 6.65) * mm, "mid": v(11.91, 6.74) * mm, "end": v(11.86, 6.82) * mm});
            skLineSegment(sketch, "E163", {"start": v(11.96, 6.65) * mm, "end": v(13.34, 6.27) * mm});
            skArc(sketch, "E164", {"start": v(12.12, 8.38) * mm, "mid": v(11.98, 8.58) * mm, "end": v(11.83, 8.78) * mm});
            skArc(sketch, "E165", {"start": v(11.86, 6.82) * mm, "mid": v(11.81, 6.91) * mm, "end": v(11.76, 7) * mm});
            skLineSegment(sketch, "E166", {"start": v(11.76, 7) * mm, "end": v(12.12, 8.38) * mm});
            skArc(sketch, "E167", {"start": v(11.83, 8.78) * mm, "mid": v(11.68, 8.98) * mm, "end": v(11.53, 9.18) * mm});
            skArc(sketch, "E168", {"start": v(10.1, 9.23) * mm, "mid": v(10.03, 9.3) * mm, "end": v(9.97, 9.38) * mm});
            skLineSegment(sketch, "E169", {"start": v(10.1, 9.23) * mm, "end": v(11.53, 9.18) * mm});
            skArc(sketch, "E170", {"start": v(9.86, 10.95) * mm, "mid": v(9.67, 11.11) * mm, "end": v(9.48, 11.27) * mm});
            skArc(sketch, "E171", {"start": v(9.97, 9.38) * mm, "mid": v(9.9, 9.45) * mm, "end": v(9.83, 9.52) * mm});
            skLineSegment(sketch, "E172", {"start": v(9.83, 9.52) * mm, "end": v(9.86, 10.95) * mm});
            skArc(sketch, "E173", {"start": v(9.48, 11.27) * mm, "mid": v(9.29, 11.43) * mm, "end": v(9.1, 11.59) * mm});
            skArc(sketch, "E174", {"start": v(7.7, 11.31) * mm, "mid": v(7.61, 11.37) * mm, "end": v(7.53, 11.42) * mm});
            skLineSegment(sketch, "E175", {"start": v(7.7, 11.31) * mm, "end": v(9.1, 11.59) * mm});
            skArc(sketch, "E176", {"start": v(7.06, 12.92) * mm, "mid": v(6.84, 13.04) * mm, "end": v(6.62, 13.16) * mm});
            skArc(sketch, "E177", {"start": v(7.53, 11.42) * mm, "mid": v(7.44, 11.48) * mm, "end": v(7.36, 11.53) * mm});
            skLineSegment(sketch, "E178", {"start": v(7.36, 11.53) * mm, "end": v(7.06, 12.92) * mm});
            skArc(sketch, "E179", {"start": v(6.62, 13.16) * mm, "mid": v(6.4, 13.27) * mm, "end": v(6.17, 13.37) * mm});
            skArc(sketch, "E180", {"start": v(4.87, 12.78) * mm, "mid": v(4.78, 12.81) * mm, "end": v(4.69, 12.85) * mm});
            skLineSegment(sketch, "E181", {"start": v(4.87, 12.78) * mm, "end": v(6.17, 13.37) * mm});
            skArc(sketch, "E182", {"start": v(3.89, 14.2) * mm, "mid": v(3.64, 14.27) * mm, "end": v(3.4, 14.33) * mm});
            skArc(sketch, "E183", {"start": v(4.69, 12.85) * mm, "mid": v(4.6, 12.88) * mm, "end": v(4.5, 12.92) * mm});
            skLineSegment(sketch, "E184", {"start": v(4.5, 12.92) * mm, "end": v(3.89, 14.2) * mm});
            skArc(sketch, "E185", {"start": v(3.4, 14.33) * mm, "mid": v(3.16, 14.38) * mm, "end": v(2.91, 14.43) * mm});
            skArc(sketch, "E186", {"start": v(1.79, 13.56) * mm, "mid": v(1.69, 13.57) * mm, "end": v(1.6, 13.58) * mm});
            skLineSegment(sketch, "E187", {"start": v(1.79, 13.56) * mm, "end": v(2.91, 14.43) * mm});
            skSolve(sketch);
        }
        {
            var Q0;
            Q0 = qSketchRegion(id + "F7", true);
            extrude(context, id + "F8", {"entities" : qUnion([Q0]), "operationType" : NewBodyOperationType.REMOVE, "endBound" : BoundingType.THROUGH_ALL, "oppositeDirection" : true, "depth" : 25 * mm, "offsetDistance" : 25 * mm});
        }
    });
